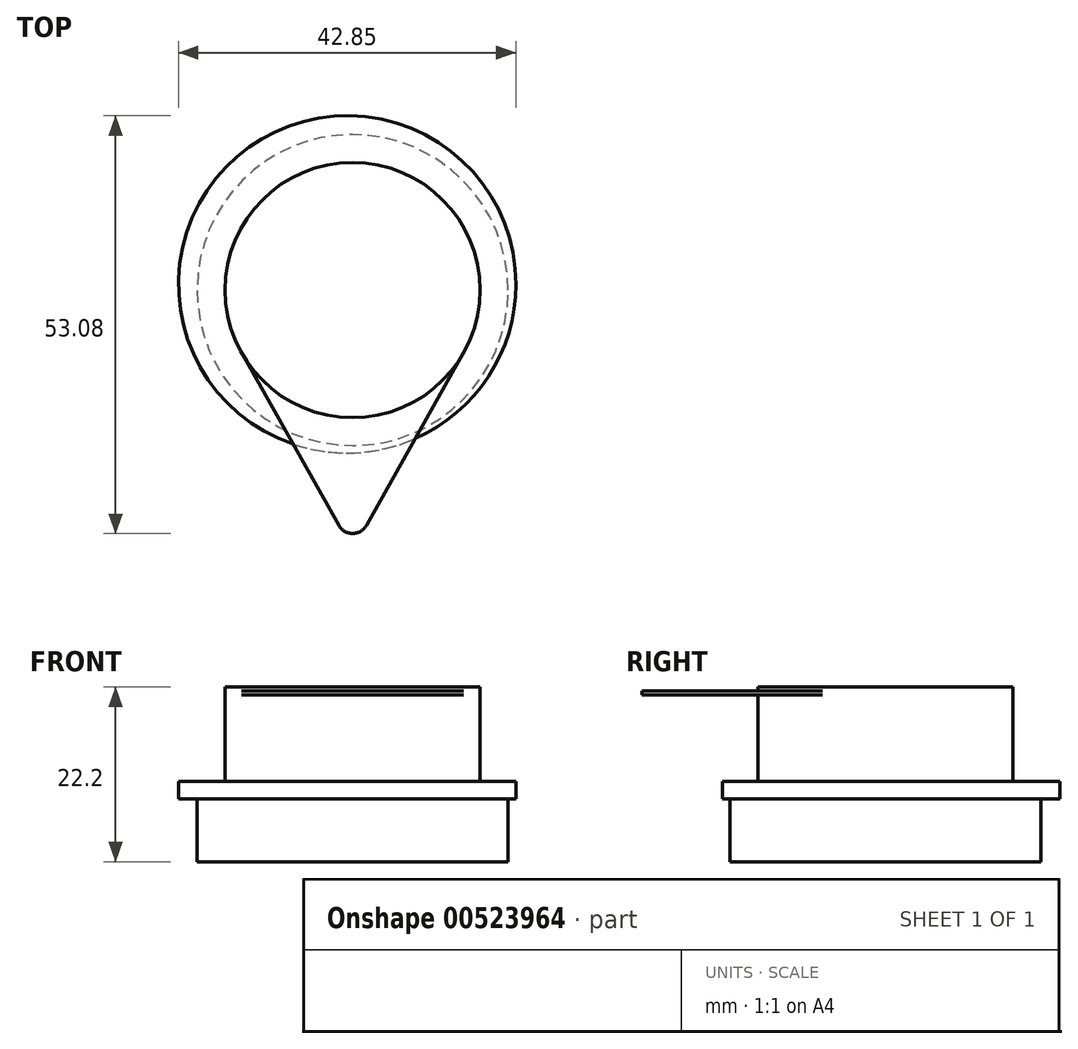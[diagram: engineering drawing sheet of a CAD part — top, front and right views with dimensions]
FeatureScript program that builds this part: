
annotation { "Feature Type Name" : "Feature", "Feature Type Description" : "" }
export const myFeature = defineFeature(function(context is Context, id is Id, definition is map)
    precondition{}
    {
        {
            var Q0;
            Q0=qCreatedBy(makeId("Top.planeOp"),FACE);
            var sketch = newSketch(context, id + "F0", { "sketchPlane" : qUnion([Q0])});
            skCircle(sketch, "E0", {"center": v(0, 0) * mm, "radius": 19.75 * mm});
            skSolve(sketch);
        }
        {
            var Q0;
            Q0 = qSketchRegion(id + "F0", true);
            extrude(context, id + "F1", {"entities" : qUnion([Q0]), "depth" : 8 * mm, "offsetDistance" : 25 * mm});
        }
        {
            var Q0;
            Q0=makeQuery(id+"F1.opExtrude","CAP_FACE",FACE,{"disambiguationData":[OSD([sQuery(id+"F0.wireOp",EDGE,"E0")])],"isStart":false});
            var sketch = newSketch(context, id + "F2", { "sketchPlane" : qUnion([Q0])});
            skCircle(sketch, "E1", {"center": v(-0.68, 0.73) * mm, "radius": 21.43 * mm});
            skSolve(sketch);
        }
        {
            var Q0;
            Q0 = qSketchRegion(id + "F2", true);
            extrude(context, id + "F3", {"entities" : qUnion([Q0]), "operationType" : NewBodyOperationType.ADD, "depth" : 2.2 * mm, "offsetDistance" : 25 * mm});
        }
        {
            var Q0;
            Q0=makeQuery(id+"F3.opExtrude","CAP_FACE",FACE,{"disambiguationData":[OSD([sQuery(id+"F2.wireOp",EDGE,"E1")])],"isStart":false});
            var sketch = newSketch(context, id + "F4", { "sketchPlane" : qUnion([Q0])});
            skCircle(sketch, "E2", {"center": v(0, 0) * mm, "radius": 16.2 * mm});
            skSolve(sketch);
        }
        {
            var Q0;
            Q0 = qSketchRegion(id + "F4", true);
            extrude(context, id + "F5", {"entities" : qUnion([Q0]), "operationType" : NewBodyOperationType.ADD, "depth" : 12 * mm, "offsetDistance" : 25 * mm});
        }
        {
            var Q0;
            Q0=makeQuery(id+"F5.opExtrude","CAP_FACE",FACE,{"disambiguationData":[OSD([sQuery(id+"F4.wireOp",EDGE,"E2")])],"isStart":false});
            cPlane(context, id + "F6", {"entities" : qUnion([Q0]), "cplaneType" : CPlaneType.OFFSET, "offset" : 1 * mm, "oppositeDirection" : true, "width" : 150 * mm, "height" : 150 * mm});
        }
        {
            var Q0;
            Q0=qCreatedBy(id+"F6.planeOp",FACE);
            var sketch = newSketch(context, id + "F7", { "sketchPlane" : qUnion([Q0])});
            skCircle(sketch, "E3.0", {"center": v(0, 0) * mm, "radius": 16.2 * mm});
            skLineSegment(sketch, "E4", {"start": v(0, 0) * mm, "end": v(0, -71.16) * mm, "construction": true});
            skLineSegment(sketch, "E5", {"start": v(-1.74, -29.9) * mm, "end": v(-14.11, -7.95) * mm});
            skLineSegment(sketch, "E6.MirrorCS", {"start": v(1.74, -29.9) * mm, "end": v(14.11, -7.95) * mm});
            skPoint(sketch, "E7.visualSharp", {"position": v(0, -33) * mm});
            skArc(sketch, "E7.filletArc", {"start": v(-1.74, -29.9) * mm, "mid": v(0, -30.93) * mm, "end": v(1.74, -29.9) * mm});
            skSolve(sketch);
        }
        {
            var Q0;
            Q0=makeQuery(id+"F3.opExtrude","CAP_FACE",FACE,{"disambiguationData":[OSD([sQuery(id+"F2.wireOp",EDGE,"E1")])],"isStart":false});
            var sketch = newSketch(context, id + "F8", { "sketchPlane" : qUnion([Q0])});
            skLineSegment(sketch, "E8", {"start": v(-1.1, -18.62) * mm, "end": v(-8, -14.09) * mm});
            skLineSegment(sketch, "E9.MirrorCS", {"start": v(1.1, -18.62) * mm, "end": v(8, -14.09) * mm});
            skPoint(sketch, "E10.visualSharp", {"position": v(0, -19.34) * mm});
            skArc(sketch, "E10.filletArc", {"start": v(-1.1, -18.62) * mm, "mid": v(0, -18.95) * mm, "end": v(1.1, -18.62) * mm});
            skSolve(sketch);
        }
        {
            var Q0;
            Q0 = qSketchRegion(id + "F7", true);
            var Q1;
            Q1 = qSketchRegion(id + "F8", true);
            var Q2;
            {var subQ0=sQuery(id+"F8.wireOp",EDGE,"E8");Q2=makeQuery(id+"F8.imprint","IMPRINT",FACE,{"disambiguationData":[TD([[makeQuery(id+"F8.imprint","IMPRINT",EDGE,{"derivedFrom":subQ0}),-1.0]])]});}
            var Q3;
            {var subQ0=sQuery(id+"F7.wireOp",EDGE,"E5");Q3=makeQuery(id+"F7.imprint","IMPRINT",FACE,{"disambiguationData":[TD([[makeQuery(id+"F7.imprint","IMPRINT",EDGE,{"derivedFrom":subQ0}),-1.0]])]});}
            loft(context, id + "F9", {"bodyType" : ToolBodyType.SURFACE, "sheetProfilesArray" : [{ "sheetProfileEntities" : qUnion([Q0]) }, { "sheetProfileEntities" : qUnion([Q1]) }], "wireProfilesArray" : [{ "wireProfileEntities" : qUnion([Q2]) }, { "wireProfileEntities" : qUnion([Q3]) }]});
        }
        {
            var Q0;
            Q0 = qSketchRegion(id + "F7", true);
            extrude(context, id + "F10", {"entities" : qUnion([Q0]), "operationType" : NewBodyOperationType.ADD, "depth" : .5 * mm, "offsetDistance" : 25 * mm});
        }
    });
